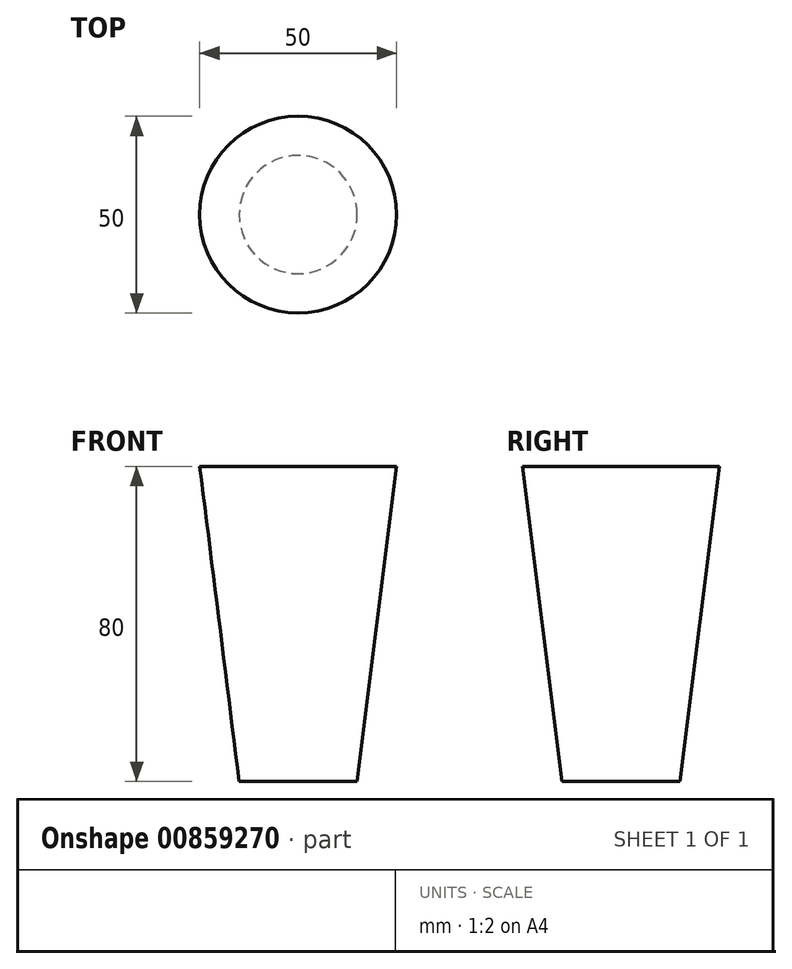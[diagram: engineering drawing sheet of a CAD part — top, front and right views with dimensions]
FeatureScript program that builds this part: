
annotation { "Feature Type Name" : "Feature", "Feature Type Description" : "" }
export const myFeature = defineFeature(function(context is Context, id is Id, definition is map)
    precondition{}
    {
        {
            var Q0;
            Q0=qCreatedBy(makeId("Front.planeOp"),FACE);
            var sketch = newSketch(context, id + "F0", { "sketchPlane" : qUnion([Q0])});
            skLineSegment(sketch, "E0", {"start": v(0, 0) * mm, "end": v(-15, 0) * mm});
            skLineSegment(sketch, "E1", {"start": v(0, 0) * mm, "end": v(0, 80) * mm});
            skLineSegment(sketch, "E2", {"start": v(0, 80) * mm, "end": v(-25, 80) * mm});
            skLineSegment(sketch, "E3", {"start": v(-25, 80) * mm, "end": v(-15, 0) * mm});
            skSolve(sketch);
        }
        {
            var Q0;
            Q0=makeQuery(id+"F0.imprint","IMPRINT",FACE,{"disambiguationData":[TD([[makeQuery(id+"F0.imprint","IMPRINT",EDGE,{"derivedFrom":sQuery(id+"F0.wireOp",EDGE,"E0")}),-1.0]])]});
            var Q1;
            Q1=sQuery(id+"F0.wireOp",EDGE,"E1");
            revolve(context, id + "F1", {"surfaceOperationType" : NewSurfaceOperationType.NEW, "entities" : qUnion([Q0]), "axis" : qUnion([Q1]), "revolveType" : RevolveType.FULL});
        }
    });
